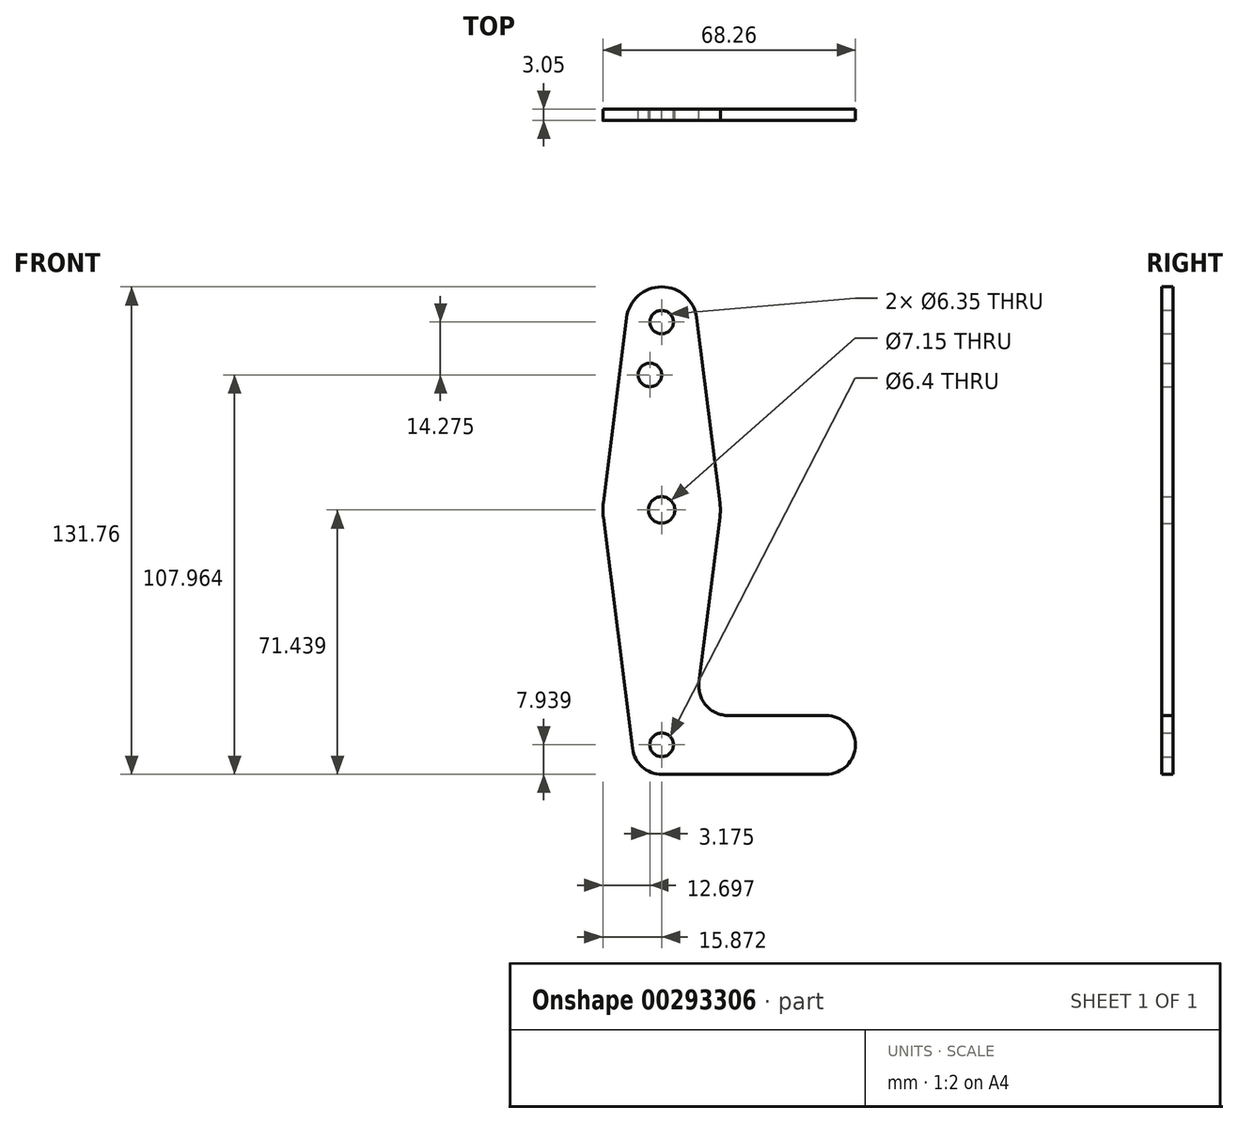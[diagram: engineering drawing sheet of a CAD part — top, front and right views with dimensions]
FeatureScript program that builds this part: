
annotation { "Feature Type Name" : "Feature", "Feature Type Description" : "" }
export const myFeature = defineFeature(function(context is Context, id is Id, definition is map)
    precondition{}
    {
        {
            var Q0;
            Q0=qCreatedBy(makeId("Front.planeOp"),FACE);
            var sketch = newSketch(context, id + "F0", { "sketchPlane" : qUnion([Q0])});
            skLineSegment(sketch, "E0", {"start": v(-49.52, 89.42) * mm, "end": v(-49.52, 38.62) * mm});
            skLineSegment(sketch, "E1", {"start": v(-49.52, 38.62) * mm, "end": v(-49.52, -24.88) * mm});
            skLineSegment(sketch, "E2", {"start": v(-49.52, -24.88) * mm, "end": v(-5.07, -24.88) * mm});
            skCircle(sketch, "E3", {"center": v(-49.52, 89.42) * mm, "radius": 9.53 * mm});
            skCircle(sketch, "E4", {"center": v(-49.52, 38.62) * mm, "radius": 15.88 * mm});
            skCircle(sketch, "E5", {"center": v(-49.52, -24.88) * mm, "radius": 7.94 * mm});
            skCircle(sketch, "E6", {"center": v(-5.07, -24.88) * mm, "radius": 7.94 * mm});
            skLineSegment(sketch, "E7", {"start": v(-58.97, 90.6) * mm, "end": v(-65.27, 40.6) * mm});
            skLineSegment(sketch, "E8", {"start": v(-40.07, 90.6) * mm, "end": v(-33.77, 40.6) * mm});
            skLineSegment(sketch, "E9", {"start": v(-65.27, 36.63) * mm, "end": v(-57.4, -25.87) * mm});
            skLineSegment(sketch, "E10", {"start": v(-33.77, 36.63) * mm, "end": v(-39.4, -8) * mm});
            skLineSegment(sketch, "E11", {"start": v(-49.52, -32.82) * mm, "end": v(-5.07, -32.82) * mm});
            skLineSegment(sketch, "E12", {"start": v(-31.5, -16.94) * mm, "end": v(-5.07, -16.94) * mm});
            skCircle(sketch, "E13", {"center": v(-49.52, 89.42) * mm, "radius": 3.18 * mm});
            skCircle(sketch, "E14", {"center": v(-49.52, 38.62) * mm, "radius": 3.58 * mm});
            skCircle(sketch, "E15", {"center": v(-49.52, -24.88) * mm, "radius": 3.2 * mm});
            skCircle(sketch, "E16", {"center": v(-52.7, 75.14) * mm, "radius": 3.18 * mm});
            skArc(sketch, "E17.filletArc", {"start": v(-39.4, -8) * mm, "mid": v(-37.47, -14.25) * mm, "end": v(-31.5, -16.94) * mm});
            skSolve(sketch);
        }
        {
            var Q0;
            Q0 = qSketchRegion(id + "F0", true);
            var Q1;
            {var subQ0=sQuery(id+"F0.wireOp",EDGE,"E5");var subQ1=sQuery(id+"F0.wireOp",EDGE,"E1");var subQ2=makeQuery(id+"F0.imprint","INTERSECT",VERTEX,{"derivedFrom":[subQ1,subQ0]});Q1=makeQuery(id+"F0.imprint","IMPRINT",FACE,{"disambiguationData":[TD([[makeQuery(id+"F0.imprint","IMPRINT",EDGE,{"disambiguationData":[TD([[subQ2,-1.0]])],"derivedFrom":subQ1}),1.0]])]});}
            extrude(context, id + "F1", {"entities" : qUnion([Q0, Q1]), "depth" : 3.05 * mm});
        }
    });
